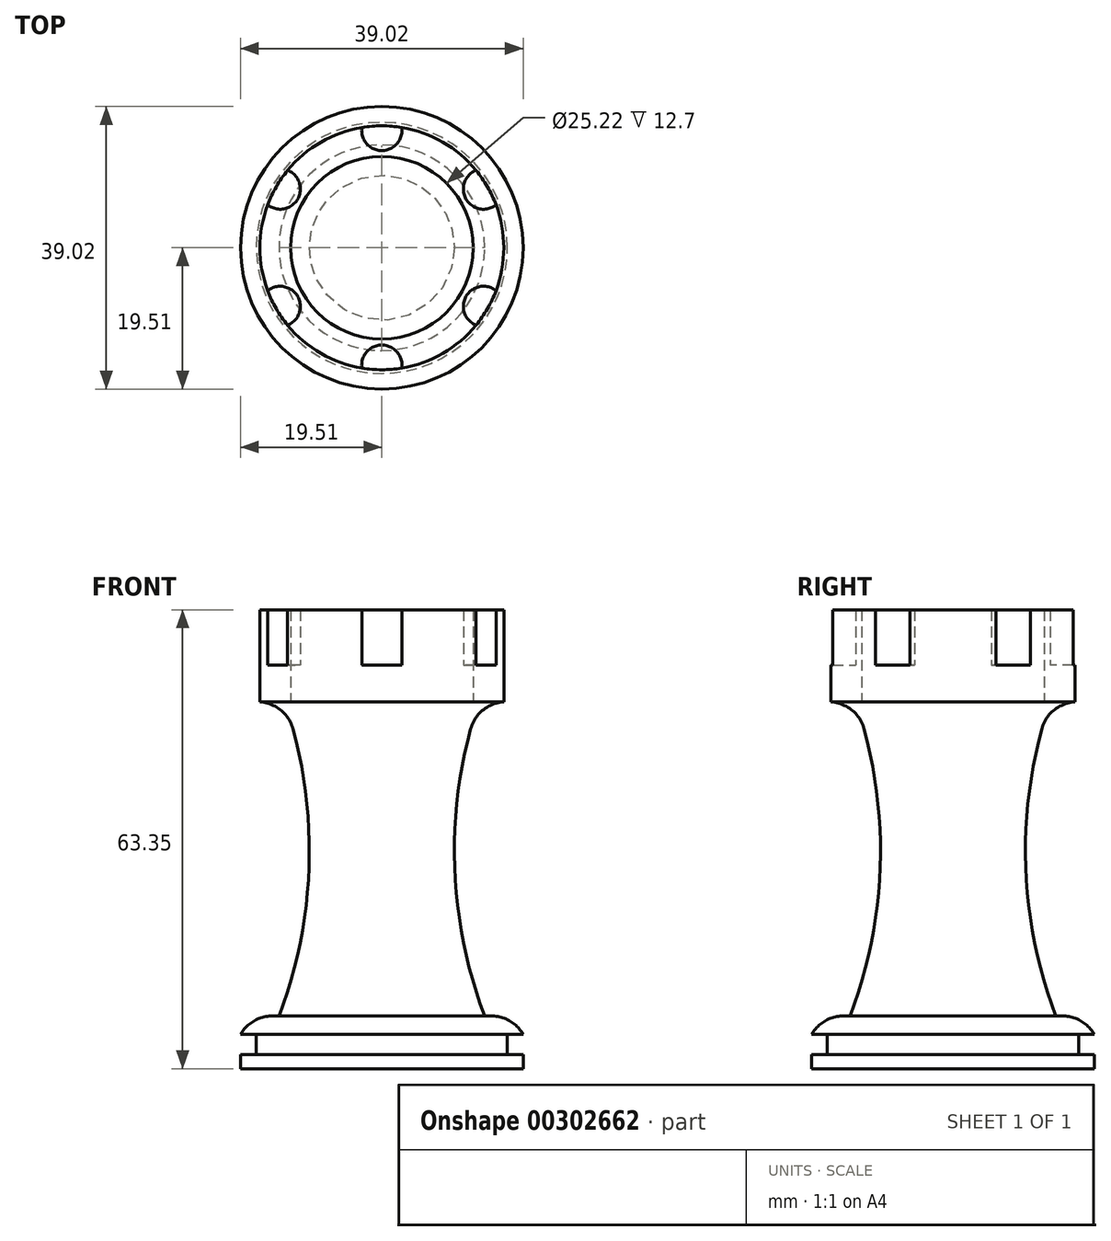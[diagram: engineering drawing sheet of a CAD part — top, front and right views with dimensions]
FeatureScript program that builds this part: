
annotation { "Feature Type Name" : "Feature", "Feature Type Description" : "" }
export const myFeature = defineFeature(function(context is Context, id is Id, definition is map)
    precondition{}
    {
        {
            var Q0;
            Q0=qCreatedBy(makeId("Front.planeOp"),FACE);
            var sketch = newSketch(context, id + "F0", { "sketchPlane" : qUnion([Q0])});
            skLineSegment(sketch, "E0", {"start": v(0, 0) * mm, "end": v(-19.5, 0) * mm});
            skLineSegment(sketch, "E1", {"start": v(-19.5, 0) * mm, "end": v(-19.5, 1.97) * mm});
            skLineSegment(sketch, "E2", {"start": v(-19.5, 1.97) * mm, "end": v(-17.34, 1.97) * mm});
            skLineSegment(sketch, "E3", {"start": v(-17.34, 1.97) * mm, "end": v(-17.34, 4.73) * mm});
            skLineSegment(sketch, "E4", {"start": v(-17.34, 4.73) * mm, "end": v(-19.5, 4.73) * mm});
            skLineSegment(sketch, "E5", {"start": v(-19.5, 4.73) * mm, "end": v(-19.5, 7.3) * mm});
            skLineSegment(sketch, "E6", {"start": v(-19.5, 7.3) * mm, "end": v(-14.78, 7.3) * mm});
            skLineSegment(sketch, "E7", {"start": v(-14.78, 7.3) * mm, "end": v(0, 7.3) * mm});
            skLineSegment(sketch, "E8", {"start": v(0, 7.3) * mm, "end": v(0, 0) * mm});
            skSolve(sketch);
        }
        {
            var Q0;
            Q0=makeQuery(id+"F0.imprint","IMPRINT",FACE,{"disambiguationData":[TD([[makeQuery(id+"F0.imprint","IMPRINT",EDGE,{"derivedFrom":sQuery(id+"F0.wireOp",EDGE,"E0")}),-1.0]])]});
            var Q1;
            Q1=sQuery(id+"F0.wireOp",EDGE,"E8");
            revolve(context, id + "F1", {"entities" : qUnion([Q0]), "axis" : qUnion([Q1]), "revolveType" : RevolveType.FULL});
        }
        {
            var Q0;
            Q0=qCreatedBy(makeId("Front.planeOp"),FACE);
            var sketch = newSketch(context, id + "F2", { "sketchPlane" : qUnion([Q0])});
            skLineSegment(sketch, "E9", {"start": v(13.4, 50.65) * mm, "end": v(0, 50.65) * mm});
            skLineSegment(sketch, "E10", {"start": v(14.2, 7.3) * mm, "end": v(0, 7.3) * mm});
            skLineSegment(sketch, "E11", {"start": v(0, 50.65) * mm, "end": v(0, 7.3) * mm});
            skArc(sketch, "E12", {"start": v(13.4, 50.65) * mm, "mid": v(10.03, 28.9) * mm, "end": v(14.2, 7.3) * mm});
            skSolve(sketch);
        }
        {
            var Q0;
            Q0=makeQuery(id+"F2.imprint","IMPRINT",FACE,{"disambiguationData":[TD([[makeQuery(id+"F2.imprint","IMPRINT",EDGE,{"derivedFrom":sQuery(id+"F2.wireOp",EDGE,"E9")}),1.0]])]});
            var sketch = newSketch(context, id + "F3", { "sketchPlane" : qUnion([Q0])});
            skSolve(sketch);
        }
        {
            var Q0;
            Q0=makeQuery(id+"F3.imprint","IMPRINT",FACE,{"disambiguationData":[TD([[makeQuery(id+"F3.imprint","IMPRINT",EDGE,{"derivedFrom":makeQuery(id+"F2.imprint","IMPRINT",EDGE,{"derivedFrom":sQuery(id+"F2.wireOp",EDGE,"E9")})}),1.0]])]});
            var Q1;
            Q1=sQuery(id+"F2.wireOp",EDGE,"E11");
            revolve(context, id + "F4", {"entities" : qUnion([Q0]), "axis" : qUnion([Q1]), "revolveType" : RevolveType.FULL});
        }
        {
            var Q0;
            Q0=makeQuery(id+"F4.opRevolve","SWEPT_FACE",FACE,{"disambiguationData":[OSD([sQuery(id+"F2.wireOp",EDGE,"E9")])]});
            var sketch = newSketch(context, id + "F5", { "sketchPlane" : qUnion([Q0])});
            skCircle(sketch, "E13", {"center": v(0, 0) * mm, "radius": 16.84 * mm});
            skSolve(sketch);
        }
        {
            var Q0;
            Q0=makeQuery(id+"F5.imprint","IMPRINT",FACE,{"disambiguationData":[TD([[makeQuery(id+"F5.imprint","IMPRINT",EDGE,{"derivedFrom":sQuery(id+"F5.wireOp",EDGE,"E13")}),1.0]])]});
            extrude(context, id + "F6", {"entities" : qUnion([Q0]), "depth" : 12.7 * mm});
        }
        {
            var Q0;
            Q0=makeQuery(id+"F6.opExtrude","CAP_EDGE",EDGE,{"disambiguationData":[OSD([sQuery(id+"F5.wireOp",EDGE,"E13")])],"isStart":true});
            fillet(context, id + "F7", {"entities" : qUnion([Q0]), "radius" : 5.08 * mm, "tangentPropagation" : true, "allowEdgeOverflow" : false});
        }
        {
            var Q0;
            Q0=makeQuery(id+"F1.opRevolve","SWEPT_FACE",FACE,{"disambiguationData":[OSD([sQuery(id+"F0.wireOp",EDGE,"E6"),sQuery(id+"F0.wireOp",EDGE,"E7")])]});
            fillet(context, id + "F8", {"entities" : qUnion([Q0]), "radius" : 5.08 * mm, "tangentPropagation" : true, "allowEdgeOverflow" : false});
        }
        {
            var Q0;
            Q0=makeQuery(id+"F6.opExtrude","CAP_FACE",FACE,{"disambiguationData":[OSD([sQuery(id+"F2.wireOp",EDGE,"E9"),sQuery(id+"F2.wireOp",EDGE,"E12"),sQuery(id+"F5.wireOp",EDGE,"E13")])],"isStart":false});
            extrude(context, id + "F9", {"entities" : qUnion([Q0]), "operationType" : NewBodyOperationType.REMOVE, "oppositeDirection" : true, "depth" : 12.7 * mm});
        }
        {
            var Q0;
            Q0=makeQuery(id+"F5.imprint","IMPRINT",FACE,{"disambiguationData":[TD([[makeQuery(id+"F5.imprint","IMPRINT",EDGE,{"derivedFrom":sQuery(id+"F5.wireOp",EDGE,"E13")}),1.0]])]});
            var sketch = newSketch(context, id + "F10", { "sketchPlane" : qUnion([Q0])});
            skCircle(sketch, "E14", {"center": v(0, 16.21) * mm, "radius": 2.78 * mm});
            skCircle(sketch, "E15.1.0", {"center": v(-14.04, 8.1) * mm, "radius": 2.78 * mm});
            skCircle(sketch, "E15.2.0", {"center": v(-14.04, -8.1) * mm, "radius": 2.78 * mm});
            skCircle(sketch, "E15.3.0", {"center": v(0, -16.21) * mm, "radius": 2.78 * mm});
            skCircle(sketch, "E15.4.0", {"center": v(14.04, -8.1) * mm, "radius": 2.78 * mm});
            skCircle(sketch, "E15.5.0", {"center": v(14.04, 8.1) * mm, "radius": 2.78 * mm});
            skPoint(sketch, "E15.center", {"position": v(0, 0) * mm});
            skCircle(sketch, "E16", {"center": v(0, 0) * mm, "radius": 12.6 * mm});
            skSolve(sketch);
        }
        {
            var Q0;
            Q0=makeQuery(id+"F10.imprint","IMPRINT",FACE,{"disambiguationData":[TD([[makeQuery(id+"F10.imprint","IMPRINT",EDGE,{"derivedFrom":makeQuery(id+"F5.imprint","IMPRINT",EDGE,{"derivedFrom":makeQuery(id+"F4.opRevolve","SWEPT_EDGE",EDGE,{"disambiguationData":[OSD([sQuery(id+"F2.wireOp",EDGE,"E9"),sQuery(id+"F2.wireOp",EDGE,"E12")])]})})}),-1.0]])]});
            var Q1;
            Q1=makeQuery(id+"F10.imprint","IMPRINT",FACE,{"disambiguationData":[TD([[makeQuery(id+"F10.imprint","IMPRINT",EDGE,{"derivedFrom":sQuery(id+"F10.wireOp",EDGE,"E16")}),-1.0]])]});
            extrude(context, id + "F11", {"entities" : qUnion([Q0, Q1]), "depth" : 12.7 * mm});
        }
        {
            var Q0;
            Q0=makeQuery(id+"F5.imprint","IMPRINT",FACE,{"disambiguationData":[TD([[makeQuery(id+"F5.imprint","IMPRINT",EDGE,{"derivedFrom":sQuery(id+"F5.wireOp",EDGE,"E13")}),1.0]])]});
            extrude(context, id + "F12", {"entities" : qUnion([Q0]), "operationType" : NewBodyOperationType.ADD, "depth" : 5.08 * mm});
        }
        {
            var Q0;
            Q0=makeQuery(id+"F4.opRevolve","SWEPT_EDGE",EDGE,{"disambiguationData":[OSD([sQuery(id+"F2.wireOp",EDGE,"E9"),sQuery(id+"F2.wireOp",EDGE,"E12")])]});
            fillet(context, id + "F13", {"entities" : qUnion([Q0]), "radius" : 5.08 * mm, "tangentPropagation" : true, "allowEdgeOverflow" : false});
        }
    });
